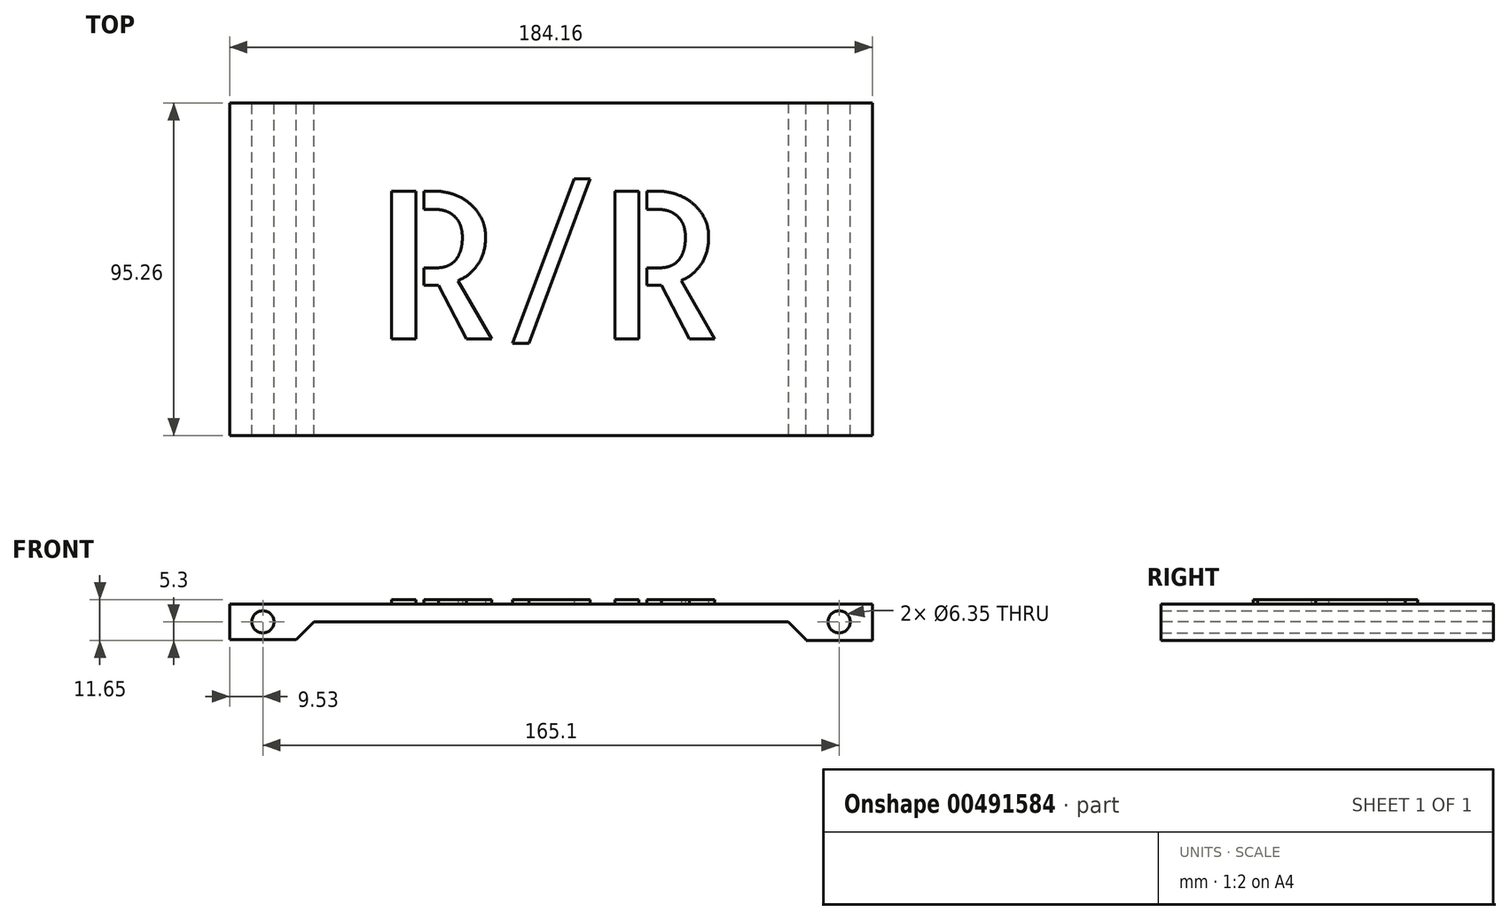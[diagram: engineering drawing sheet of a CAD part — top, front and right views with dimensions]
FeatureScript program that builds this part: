
annotation { "Feature Type Name" : "Feature", "Feature Type Description" : "" }
export const myFeature = defineFeature(function(context is Context, id is Id, definition is map)
    precondition{}
    {
        {
            var Q0;
            Q0=qCreatedBy(makeId("Front.planeOp"),FACE);
            var sketch = newSketch(context, id + "F0", { "sketchPlane" : qUnion([Q0])});
            skLineSegment(sketch, "E0.bottom", {"start": v(-92.08, 2.54) * mm, "end": v(92.08, 2.54) * mm});
            skLineSegment(sketch, "E0.top", {"start": v(-92.08, -2.54) * mm, "end": v(92.08, -2.54) * mm});
            skLineSegment(sketch, "E0.left", {"start": v(-92.08, 2.54) * mm, "end": v(-92.08, -2.54) * mm});
            skLineSegment(sketch, "E0.right", {"start": v(92.08, 2.54) * mm, "end": v(92.08, -2.54) * mm});
            skPoint(sketch, "E0.middle", {"position": v(0, 0) * mm});
            skLineSegment(sketch, "E1.bottom", {"start": v(-92.08, -2.54) * mm, "end": v(-73.03, -2.54) * mm});
            skLineSegment(sketch, "E1.top", {"start": v(-92.08, -7.62) * mm, "end": v(-73.03, -7.62) * mm});
            skLineSegment(sketch, "E1.left", {"start": v(-92.08, -2.54) * mm, "end": v(-92.08, -7.62) * mm});
            skLineSegment(sketch, "E1.right", {"start": v(-73.03, -2.54) * mm, "end": v(-73.03, -7.62) * mm});
            skCircle(sketch, "E2", {"center": v(-82.55, -2.54) * mm, "radius": 3.18 * mm});
            skLineSegment(sketch, "E3.bottom", {"start": v(92.08, -2.54) * mm, "end": v(73.03, -2.54) * mm});
            skLineSegment(sketch, "E3.top", {"start": v(92.08, -7.84) * mm, "end": v(73.03, -7.84) * mm});
            skLineSegment(sketch, "E3.left", {"start": v(92.08, -2.54) * mm, "end": v(92.08, -7.84) * mm});
            skLineSegment(sketch, "E3.right", {"start": v(73.03, -2.54) * mm, "end": v(73.03, -7.84) * mm});
            skCircle(sketch, "E4", {"center": v(82.55, -2.54) * mm, "radius": 3.18 * mm});
            skSolve(sketch);
        }
        {
            var Q0;
            Q0=qSketchRegion(id+"F0",true);
            extrude(context, id + "F1", {"entities" : qUnion([Q0]), "endBound" : BoundingType.SYMMETRIC, "depth" : 95.25 * mm});
        }
        {
            var Q0;
            Q0=makeQuery(id+"F1.opExtrude","SWEPT_EDGE",EDGE,{"disambiguationData":[OSD([sQuery(id+"F0.wireOp",EDGE,"E0.top"),sQuery(id+"F0.wireOp",EDGE,"E1.bottom"),sQuery(id+"F0.wireOp",EDGE,"E1.right")])]});
            var Q1;
            Q1=makeQuery(id+"F1.opExtrude","SWEPT_EDGE",EDGE,{"disambiguationData":[OSD([sQuery(id+"F0.wireOp",EDGE,"E0.top"),sQuery(id+"F0.wireOp",EDGE,"E3.bottom"),sQuery(id+"F0.wireOp",EDGE,"E3.right")])]});
            chamfer(context, id + "F2", {"entities" : qUnion([Q0, Q1]), "width" : 5.08 * mm, "tangentPropagation" : true});
        }
        {
            var Q0;
            Q0=makeQuery(id+"F1.opExtrude","SWEPT_FACE",FACE,{"disambiguationData":[OSD([sQuery(id+"F0.wireOp",EDGE,"E0.bottom")])]});
            var sketch = newSketch(context, id + "F3", { "sketchPlane" : qUnion([Q0])});
            skText(sketch, "E5", { "text": "R/R", "fontName": "AllertaStencil-Regular.ttf"});
            const initialGuessF3  = {"E5": [-0.05081, -0.0199, 1, 0, 0.0423]};
            skSetInitialGuess(sketch, initialGuessF3);
            skSolve(sketch);
        }
        {
            var Q0;
            Q0=qSketchRegion(id+"F3",true);
            extrude(context, id + "F4", {"entities" : qUnion([Q0]), "operationType" : NewBodyOperationType.ADD, "endBound" : BoundingType.SYMMETRIC, "depth" : 2.54 * mm});
        }
    });
